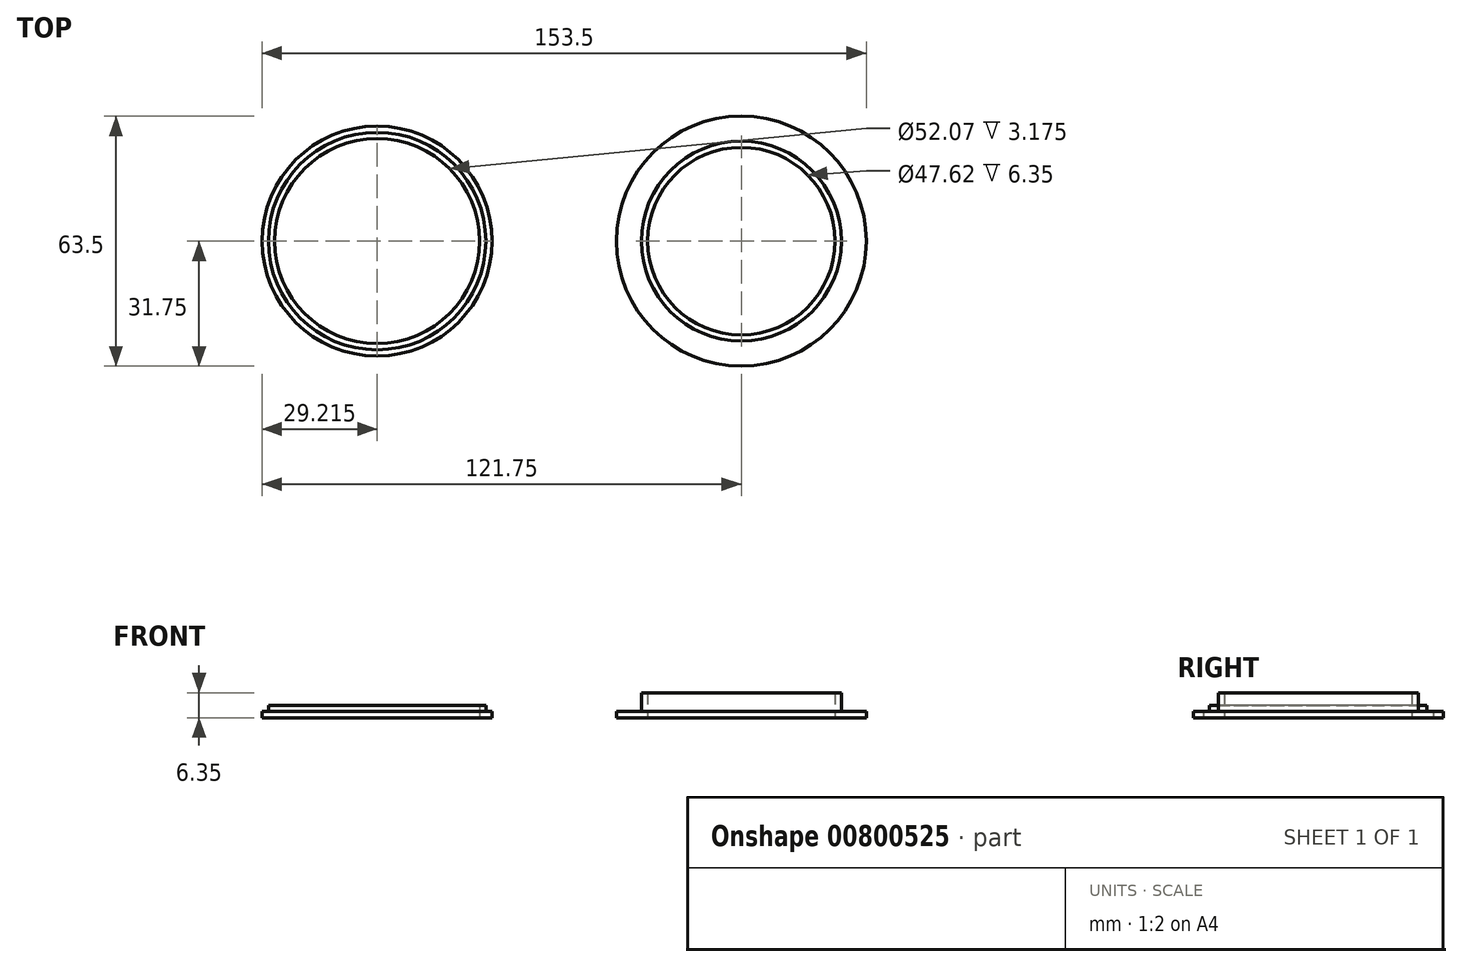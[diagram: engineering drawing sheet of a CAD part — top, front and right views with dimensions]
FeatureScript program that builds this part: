
annotation { "Feature Type Name" : "Feature", "Feature Type Description" : "" }
export const myFeature = defineFeature(function(context is Context, id is Id, definition is map)
    precondition{}
    {
        {
            var Q0;
            Q0=qCreatedBy(makeId("Top.planeOp"),FACE);
            var sketch = newSketch(context, id + "F0", { "sketchPlane" : qUnion([Q0])});
            skCircle(sketch, "E0", {"center": v(0, 0) * mm, "radius": 25.4 * mm});
            skCircle(sketch, "E1", {"center": v(0, 0) * mm, "radius": 23.81 * mm});
            skCircle(sketch, "E2", {"center": v(0, 0) * mm, "radius": 31.75 * mm});
            skSolve(sketch);
        }
        {
            var Q0;
            Q0=makeQuery(id+"F0.imprint","IMPRINT",FACE,{"disambiguationData":[TD([[makeQuery(id+"F0.imprint","IMPRINT",EDGE,{"derivedFrom":sQuery(id+"F0.wireOp",EDGE,"E0")}),-1.0]])]});
            extrude(context, id + "F1", {"entities" : qUnion([Q0]), "depth" : 1.59 * mm, "offsetDistance" : 25.4 * mm});
        }
        {
            var Q0;
            Q0=makeQuery(id+"F0.imprint","IMPRINT",FACE,{"disambiguationData":[TD([[makeQuery(id+"F0.imprint","IMPRINT",EDGE,{"derivedFrom":sQuery(id+"F0.wireOp",EDGE,"E0")}),1.0]])]});
            extrude(context, id + "F2", {"entities" : qUnion([Q0]), "operationType" : NewBodyOperationType.ADD, "depth" : 6.35 * mm, "offsetDistance" : 25.4 * mm});
        }
        {
            var Q0;
            Q0=qCreatedBy(makeId("Top.planeOp"),FACE);
            var sketch = newSketch(context, id + "F3", { "sketchPlane" : qUnion([Q0])});
            skCircle(sketch, "E3", {"center": v(-92.54, 0) * mm, "radius": 26.04 * mm});
            skCircle(sketch, "E4", {"center": v(-92.54, 0) * mm, "radius": 27.62 * mm});
            skCircle(sketch, "E5", {"center": v(-92.54, 0) * mm, "radius": 29.21 * mm});
            skSolve(sketch);
        }
        {
            var Q0;
            Q0=makeQuery(id+"F3.imprint","IMPRINT",FACE,{"disambiguationData":[TD([[makeQuery(id+"F3.imprint","IMPRINT",EDGE,{"derivedFrom":sQuery(id+"F3.wireOp",EDGE,"E3")}),-1.0]])]});
            extrude(context, id + "F4", {"entities" : qUnion([Q0]), "depth" : 3.17 * mm, "offsetDistance" : 25.4 * mm});
        }
        {
            var Q0;
            Q0=makeQuery(id+"F3.imprint","IMPRINT",FACE,{"disambiguationData":[TD([[makeQuery(id+"F3.imprint","IMPRINT",EDGE,{"derivedFrom":sQuery(id+"F3.wireOp",EDGE,"E4")}),-1.0]])]});
            extrude(context, id + "F5", {"entities" : qUnion([Q0]), "operationType" : NewBodyOperationType.ADD, "depth" : 1.59 * mm, "offsetDistance" : 25.4 * mm});
        }
    });
